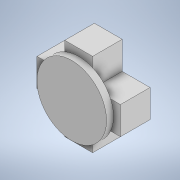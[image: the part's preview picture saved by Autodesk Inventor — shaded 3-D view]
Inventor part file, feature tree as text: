
AUTODESK INVENTOR PART (.ipt)
format: ipt  version: 2020.1 (Build 241239000, 239)  size: 128,000 bytes
history: native  units: mm
features: extrude x2, sketch x2
ambient origin geometry x8: Origin, YZ Plane, XZ Plane, XY Plane, X Axis, Y Axis, Z Axis, Center Point
bodies: Solid1 (feature_tree)
feature tree (4):
  extrude  "Extrusion1"  Depth=2.0mm
  extrude  "Extrusion2"  Depth=1.0mm
  sketch  "Sketch1"  dims[d2=2.0mm d3=2.0mm]
  sketch  "Sketch2"  dims[d4=2.0mm d5=2.0mm d6=2.0mm d7=2.0mm d8=2.0mm d9=2.0mm d10=4.25mm d11=0.0mm d12=10.0mm d13=1.0mm d14=0.0mm]
